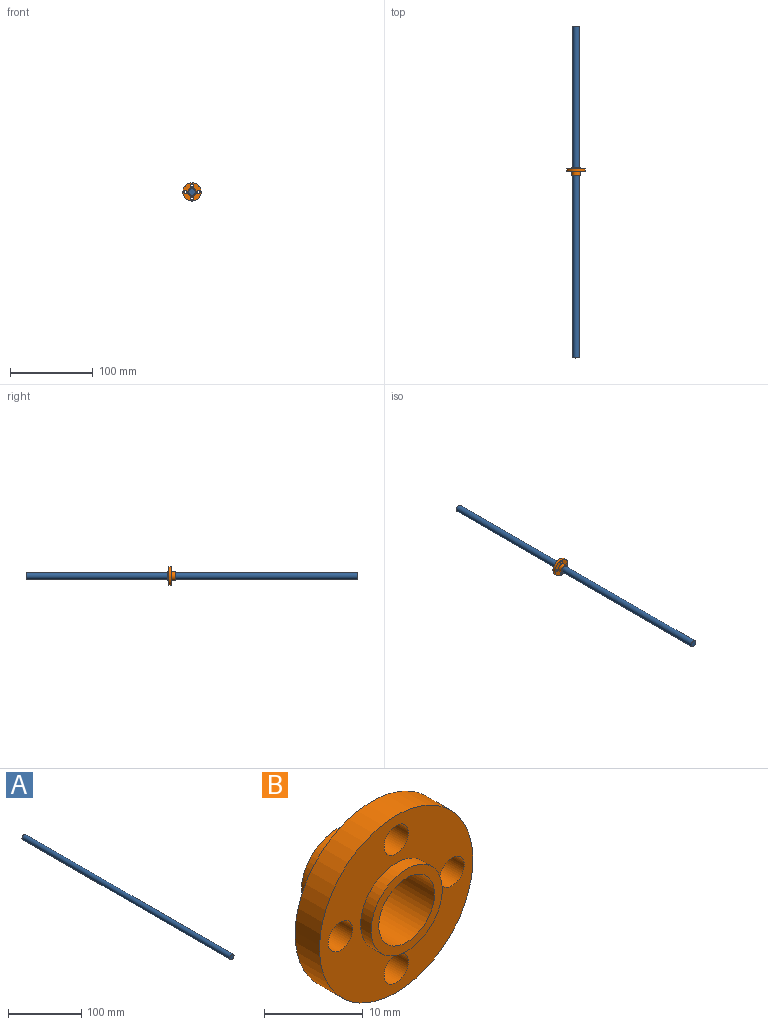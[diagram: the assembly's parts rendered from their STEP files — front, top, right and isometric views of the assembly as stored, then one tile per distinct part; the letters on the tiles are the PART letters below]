
ASSEMBLY  parts=2 mates=1
PART A: 3 faces, bbox 8x400x8 mm
  f0: cylinder r=4mm len=400mm, axis (0,1,0), area 10053.1mm2, adj f1,f2
  f1: plane 8x8mm, normal (0,-1,0), area 50.3mm2, adj f0
  f2: plane 8x8mm, normal (0,1,0), area 50.3mm2, adj f0
PART B: 12 faces, bbox 22x10x22 mm
  f0: cylinder r=1.75mm len=3.5mm, axis (0,1,0), area 38.5mm2, adj f5,f6
  f1: cylinder r=1.75mm len=3.5mm, axis (0,1,0), area 38.5mm2, adj f5,f6
  f2: cylinder r=1.75mm len=3.5mm, axis (0,1,0), area 38.5mm2, adj f5,f6
  f3: cylinder r=1.75mm len=3.5mm, axis (0,1,0), area 38.5mm2, adj f5,f6
  f4: cylinder r=11mm len=22mm, axis (0,1,0), area 241.9mm2, adj f5,f6
  f5: plane 22x22mm, normal (0,-1,0), area 259.9mm2, adj f0,f1,f2,f3,f4,f7
  f6: plane 22x22mm, normal (0,1,0), area 259.9mm2, adj f0,f1,f2,f3,f4,f10
  f7: cylinder r=5.1mm len=10.2mm, axis (0,1,0), area 48.1mm2, adj f5,f9
  f8: cylinder r=4mm len=10mm, axis (0,1,0), area 251.3mm2, adj f9,f11
  f9: plane 10.2x10.2mm, normal (0,-1,0), area 31.4mm2, adj f7,f8
  f10: cylinder r=5.1mm len=10.2mm, axis (0,-1,0), area 160.2mm2, adj f6,f11
  f11: plane 10.2x10.2mm, normal (0,1,0), area 31.4mm2, adj f8,f10
PLACE A t=(-148.92,-42.69,-57.05)mm
PLACE B rot(axis=(1,0,0),180deg) t=(-148.92,-217.95,-57.05)mm
MATE slider B.f8 <-> A.f0  axis (0,-1,0) through (-148.92,-212.95,-57.05)mm
